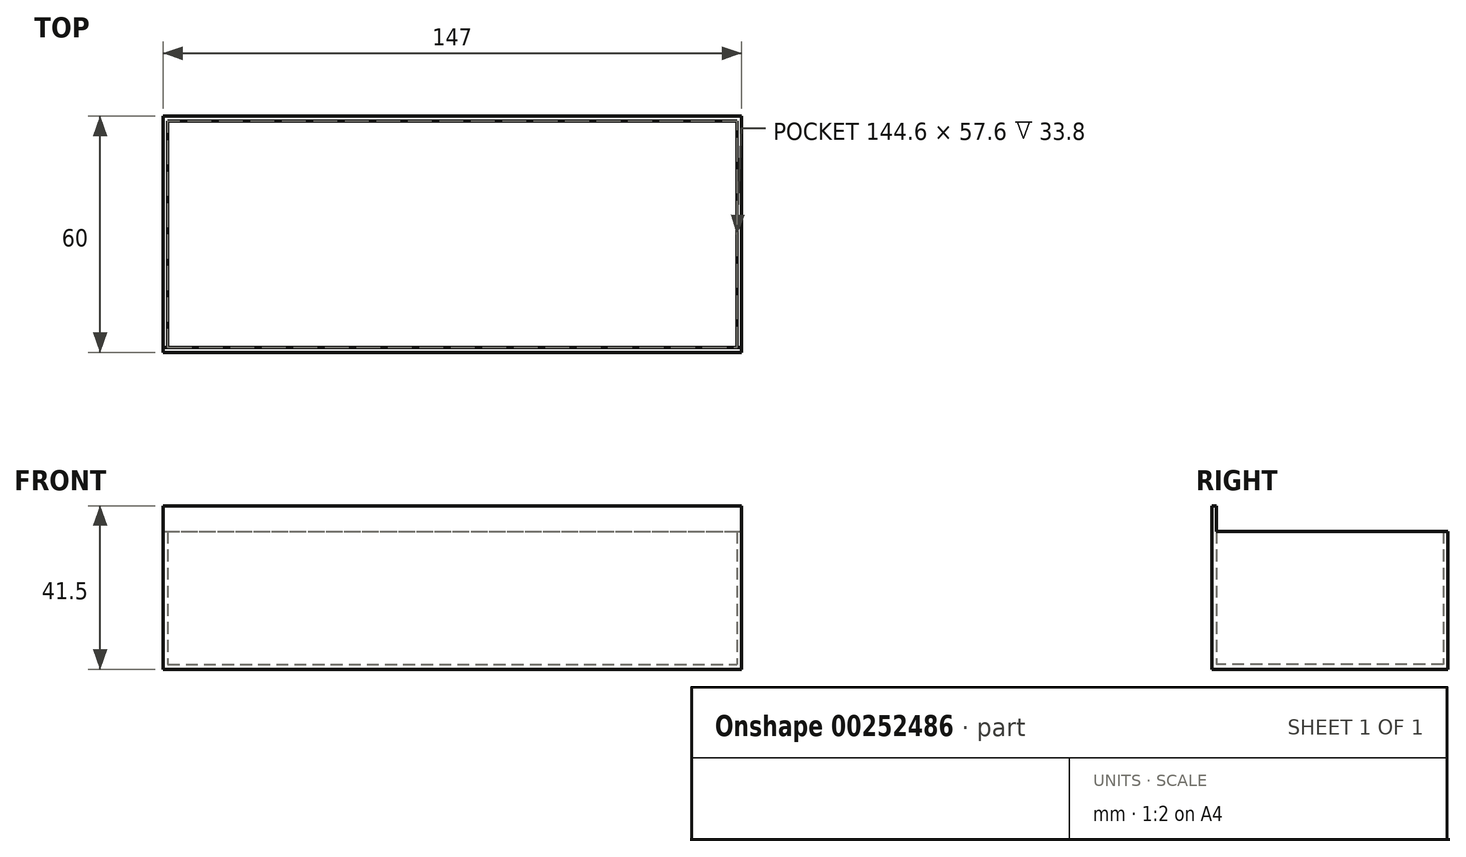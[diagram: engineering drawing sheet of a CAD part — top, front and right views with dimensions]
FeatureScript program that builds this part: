
annotation { "Feature Type Name" : "Feature", "Feature Type Description" : "" }
export const myFeature = defineFeature(function(context is Context, id is Id, definition is map)
    precondition{}
    {
        {
            var Q0;
            Q0=qCreatedBy(makeId("Top.planeOp"),FACE);
            var sketch = newSketch(context, id + "F0", { "sketchPlane" : qUnion([Q0])});
            skLineSegment(sketch, "E0.bottom", {"start": v(-71.2, 15.6) * mm, "end": v(75.8, 15.6) * mm});
            skLineSegment(sketch, "E0.top", {"start": v(-71.2, -44.4) * mm, "end": v(75.8, -44.4) * mm});
            skLineSegment(sketch, "E0.left", {"start": v(-71.2, 15.6) * mm, "end": v(-71.2, -44.4) * mm});
            skLineSegment(sketch, "E0.right", {"start": v(75.8, 15.6) * mm, "end": v(75.8, -44.4) * mm});
            skSolve(sketch);
        }
        {
            var Q0;
            Q0=makeQuery(id+"F0.imprint","IMPRINT",FACE,{"disambiguationData":[TD([[makeQuery(id+"F0.imprint","IMPRINT",EDGE,{"derivedFrom":sQuery(id+"F0.wireOp",EDGE,"E0.bottom")}),-1.0]])]});
            extrude(context, id + "F1", {"entities" : qUnion([Q0]), "depth" : 35 * mm});
        }
        {
            var Q0;
            Q0=makeQuery(id+"F1.opExtrude","CAP_FACE",FACE,{"disambiguationData":[OSD([sQuery(id+"F0.wireOp",EDGE,"E0.bottom"),sQuery(id+"F0.wireOp",EDGE,"E0.top"),sQuery(id+"F0.wireOp",EDGE,"E0.left"),sQuery(id+"F0.wireOp",EDGE,"E0.right")])],"isStart":false});
            var sketch = newSketch(context, id + "F2", { "sketchPlane" : qUnion([Q0])});
            skLineSegment(sketch, "E1.bottom", {"start": v(-71.2, -44.4) * mm, "end": v(75.8, -44.4) * mm});
            skLineSegment(sketch, "E1.top", {"start": v(-71.2, -42.8) * mm, "end": v(75.8, -42.8) * mm});
            skLineSegment(sketch, "E1.left", {"start": v(-71.2, -44.4) * mm, "end": v(-71.2, -42.8) * mm});
            skLineSegment(sketch, "E1.right", {"start": v(75.8, -44.4) * mm, "end": v(75.8, -42.8) * mm});
            skSolve(sketch);
        }
        {
            var Q0;
            Q0=makeQuery(id+"F2.imprint","IMPRINT",FACE,{"disambiguationData":[TD([[makeQuery(id+"F2.imprint","IMPRINT",EDGE,{"derivedFrom":sQuery(id+"F2.wireOp",EDGE,"E1.bottom")}),1.0]])]});
            extrude(context, id + "F3", {"entities" : qUnion([Q0]), "operationType" : NewBodyOperationType.ADD, "depth" : 6.5 * mm});
        }
        {
            var Q0;
            Q0=makeQuery(id+"F1.opExtrude","CAP_FACE",FACE,{"disambiguationData":[OSD([sQuery(id+"F0.wireOp",EDGE,"E0.bottom"),sQuery(id+"F0.wireOp",EDGE,"E0.top"),sQuery(id+"F0.wireOp",EDGE,"E0.left"),sQuery(id+"F0.wireOp",EDGE,"E0.right")])],"isStart":false});
            shell(context, id + "F4", {"entities" : qUnion([Q0]), "thickness" : 1.2 * mm});
        }
        {
            var Q0;
            Q0=makeQuery(id+"F3.opExtrude","SWEPT_FACE",FACE,{"disambiguationData":[OSD([sQuery(id+"F2.wireOp",EDGE,"E1.top")])]});
            extrude(context, id + "F5", {"entities" : qUnion([Q0]), "operationType" : NewBodyOperationType.REMOVE, "oppositeDirection" : true, "depth" : 0.4 * mm});
        }
    });
